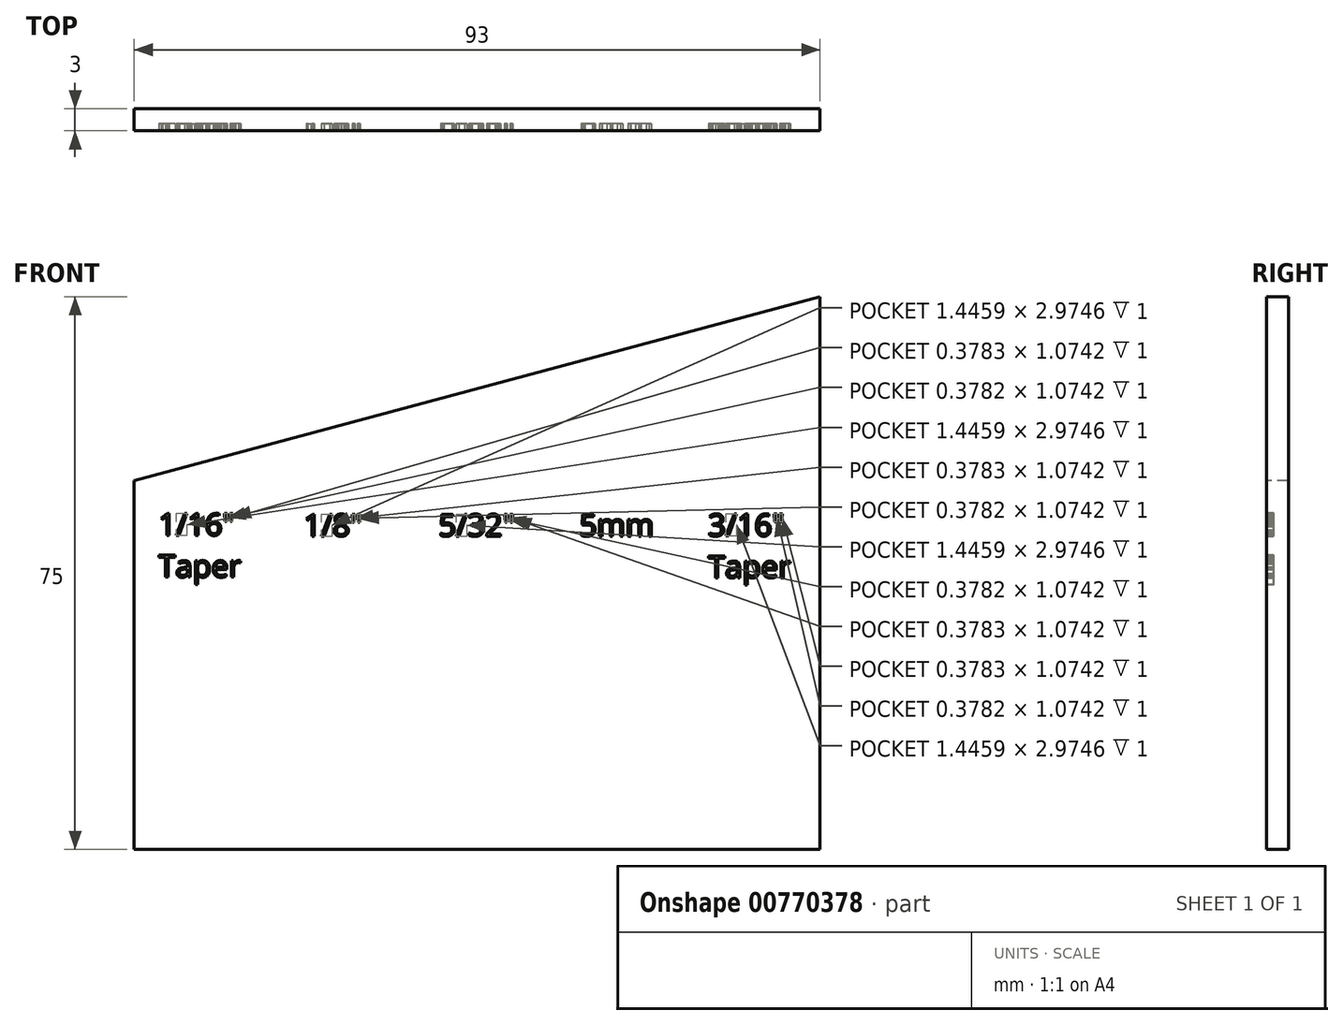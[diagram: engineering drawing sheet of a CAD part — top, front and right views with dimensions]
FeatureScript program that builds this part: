
annotation { "Feature Type Name" : "Feature", "Feature Type Description" : "" }
export const myFeature = defineFeature(function(context is Context, id is Id, definition is map)
    precondition{}
    {
        {
            var Q0;
            Q0=qCreatedBy(makeId("Front.planeOp"),FACE);
            var sketch = newSketch(context, id + "F0", { "sketchPlane" : qUnion([Q0])});
            skLineSegment(sketch, "E0.bottom", {"start": v(0, 0) * mm, "end": v(93, 0) * mm});
            skLineSegment(sketch, "E0.left", {"start": v(0, 0) * mm, "end": v(0, 50) * mm});
            skLineSegment(sketch, "E0.right", {"start": v(93, 0) * mm, "end": v(93, 75) * mm});
            skLineSegment(sketch, "E1", {"start": v(93, 75) * mm, "end": v(0, 50) * mm});
            skLineSegment(sketch, "E2.1.0.0", {"start": v(18.6, 0) * mm, "end": v(18.6, 50) * mm, "construction": true});
            skLineSegment(sketch, "E2.2.0.0", {"start": v(37.2, 0) * mm, "end": v(37.2, 50) * mm, "construction": true});
            skLineSegment(sketch, "E2.3.0.0", {"start": v(55.8, 0) * mm, "end": v(55.8, 50) * mm, "construction": true});
            skLineSegment(sketch, "E2.4.0.0", {"start": v(74.4, 0) * mm, "end": v(74.4, 50) * mm, "construction": true});
            skLineSegment(sketch, "E2.5.0.0", {"start": v(93, 0) * mm, "end": v(93, 50) * mm, "construction": true});
            skLineSegment(sketch, "E2.direction1", {"start": v(0, 0) * mm, "end": v(18.6, 0) * mm, "construction": true});
            skSolve(sketch);
        }
        {
            var Q0;
            Q0=makeQuery(id+"F0.imprint","IMPRINT",FACE,{"disambiguationData":[TD([[makeQuery(id+"F0.imprint","IMPRINT",EDGE,{"derivedFrom":sQuery(id+"F0.wireOp",EDGE,"E0.bottom")}),1.0]])]});
            extrude(context, id + "F1", {"entities" : qUnion([Q0]), "oppositeDirection" : true, "depth" : 3 * mm, "offsetDistance" : 25 * mm});
        }
        {
            var Q0;
            Q0=qCreatedBy(makeId("Front.planeOp"),FACE);
            var sketch = newSketch(context, id + "F2", { "sketchPlane" : qUnion([Q0])});
            skText(sketch, "E3", { "text": "1/16\"\nTaper", "fontName": "OpenSans-Regular.ttf"});
            skText(sketch, "E4", { "text": "1/8\"", "fontName": "OpenSans-Regular.ttf"});
            skText(sketch, "E5", { "text": "5/32\"", "fontName": "OpenSans-Regular.ttf"});
            skText(sketch, "E6", { "text": "5mm", "fontName": "OpenSans-Regular.ttf"});
            skText(sketch, "E7", { "text": "3/16\"\nTaper", "fontName": "OpenSans-Regular.ttf"});
            const initialGuessF2  = {"E3": [0.00328, 0.0426, 1, 0, 0.003], "E4": [0.02298, 0.0425, 1, 0, 0.003], "E5": [0.04127, 0.0425, 1, 0, 0.003], "E6": [0.06037, 0.0425, 1, 0, 0.003], "E7": [0.07783, 0.04252, 1, 0, 0.003]};
            skSetInitialGuess(sketch, initialGuessF2);
            skSolve(sketch);
        }
        {
            var Q0;
            Q0 = qSketchRegion(id + "F2", true);
            extrude(context, id + "F3", {"entities" : qUnion([Q0]), "operationType" : NewBodyOperationType.REMOVE, "oppositeDirection" : true, "depth" : 1 * mm, "offsetDistance" : 25 * mm});
        }
    });
